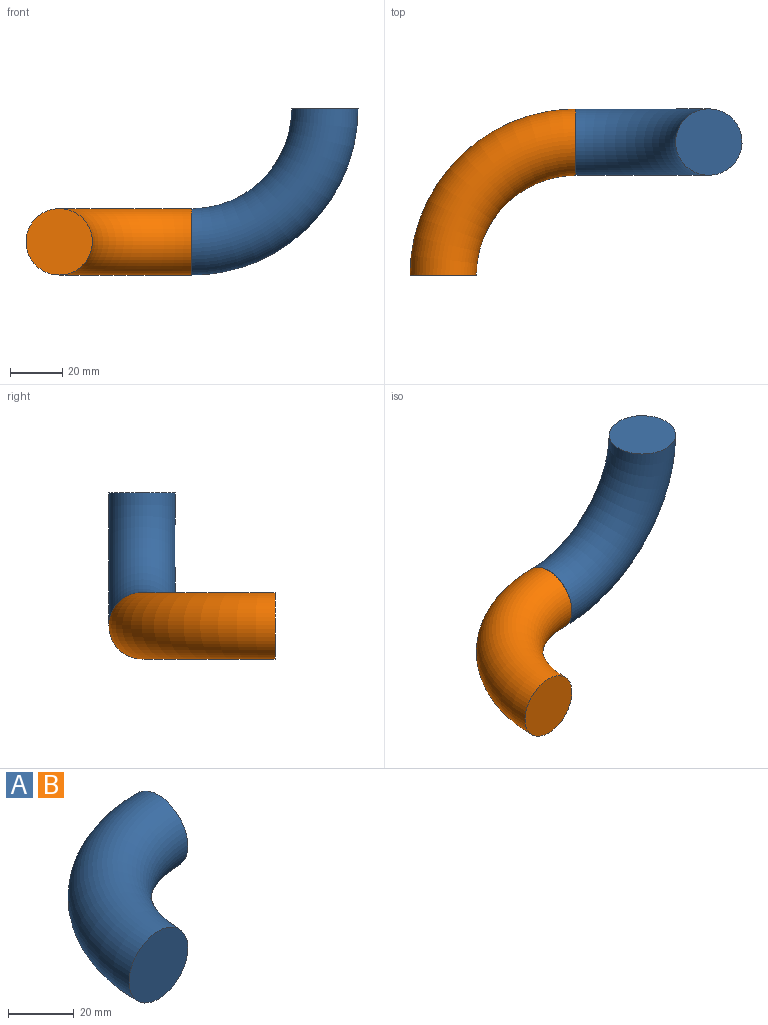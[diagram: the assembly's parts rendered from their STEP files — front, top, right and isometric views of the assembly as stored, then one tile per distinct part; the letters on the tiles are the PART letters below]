
ASSEMBLY  parts=2 mates=1
PART A: 3 faces, bbox 68.7x68.7x25.4 mm
  f0: plane 25.4x25.4mm, normal (0,-1,0), area 506.7mm2, adj f2
  f1: plane 25.4x25.4mm, normal (1,0,0), area 506.7mm2, adj f2
  f2: torus R=50.8mm, axis (0,0,-1), area 6367.5mm2, adj f0,f1
PART B: same geometry as A
PLACE A rot(axis=(0,-0.71,0.71),180deg) t=(101.6,50.8,50.8)mm
PLACE B at identity
MATE parallel A.f1 <-> B.f1  axis (-1,0,0) through (50.8,50.8,0)mm
